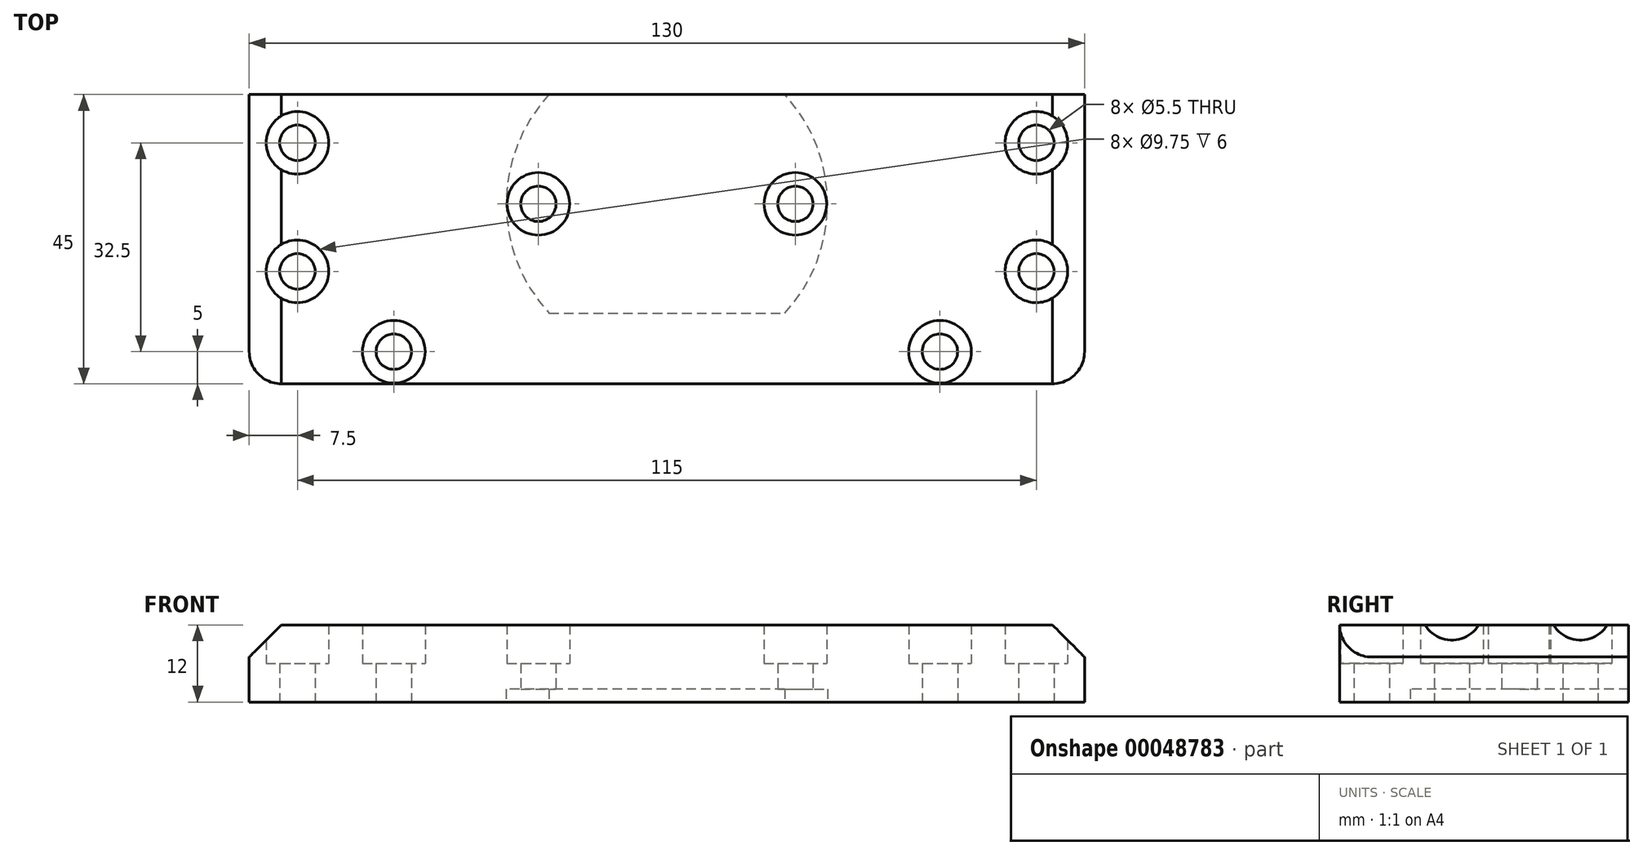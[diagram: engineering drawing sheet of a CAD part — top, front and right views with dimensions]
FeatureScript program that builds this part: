
annotation { "Feature Type Name" : "Feature", "Feature Type Description" : "" }
export const myFeature = defineFeature(function(context is Context, id is Id, definition is map)
    precondition{}
    {
        {
            var Q0;
            Q0=qCreatedBy(makeId("Top.planeOp"),FACE);
            var sketch = newSketch(context, id + "F0", { "sketchPlane" : qUnion([Q0])});
            skLineSegment(sketch, "E0.bottom", {"start": v(65, -22.5) * mm, "end": v(-65, -22.5) * mm});
            skLineSegment(sketch, "E0.top", {"start": v(65, 22.5) * mm, "end": v(-65, 22.5) * mm});
            skLineSegment(sketch, "E0.left", {"start": v(65, -22.5) * mm, "end": v(65, 22.5) * mm});
            skLineSegment(sketch, "E0.right", {"start": v(-65, -22.5) * mm, "end": v(-65, 22.5) * mm});
            skPoint(sketch, "E0.middle", {"position": v(0, 0) * mm});
            skSolve(sketch);
        }
        {
            var Q0;
            Q0=makeQuery(id+"F0.imprint","IMPRINT",FACE,{"disambiguationData":[TD([[makeQuery(id+"F0.imprint","IMPRINT",EDGE,{"derivedFrom":sQuery(id+"F0.wireOp",EDGE,"E0.bottom")}),-1.0]])]});
            extrude(context, id + "F1", {"entities" : qUnion([Q0]), "depth" : 12 * mm});
        }
        {
            var Q0;
            Q0=makeQuery(id+"F1.opExtrude","SWEPT_EDGE",EDGE,{"disambiguationData":[OSD([sQuery(id+"F0.wireOp",EDGE,"E0.bottom"),sQuery(id+"F0.wireOp",EDGE,"E0.left")])]});
            var Q1;
            Q1=makeQuery(id+"F1.opExtrude","SWEPT_EDGE",EDGE,{"disambiguationData":[OSD([sQuery(id+"F0.wireOp",EDGE,"E0.bottom"),sQuery(id+"F0.wireOp",EDGE,"E0.right")])]});
            fillet(context, id + "F2", {"entities" : qUnion([Q0, Q1]), "radius" : 5 * mm, "tangentPropagation" : true, "allowEdgeOverflow" : false});
        }
        {
            var Q0;
            Q0=makeQuery(id+"F1.opExtrude","CAP_FACE",FACE,{"disambiguationData":[OSD([sQuery(id+"F0.wireOp",EDGE,"E0.bottom"),sQuery(id+"F0.wireOp",EDGE,"E0.top"),sQuery(id+"F0.wireOp",EDGE,"E0.left"),sQuery(id+"F0.wireOp",EDGE,"E0.right")])],"isStart":false});
            var sketch = newSketch(context, id + "F3", { "sketchPlane" : qUnion([Q0])});
            skPoint(sketch, "E1", {"position": v(-57.5, -5) * mm});
            skPoint(sketch, "E2.0.1.0", {"position": v(-57.5, 15) * mm});
            skPoint(sketch, "E2.1.0.0", {"position": v(57.5, -5) * mm});
            skPoint(sketch, "E2.1.1.0", {"position": v(57.5, 15) * mm});
            skLineSegment(sketch, "E2.direction1", {"start": v(-57.5, -5) * mm, "end": v(57.5, -5) * mm, "construction": true});
            skLineSegment(sketch, "E2.direction2", {"start": v(-57.5, -5) * mm, "end": v(-57.5, 15) * mm, "construction": true});
            skPoint(sketch, "E3", {"position": v(-42.5, -17.5) * mm});
            skPoint(sketch, "E4.MirrorP", {"position": v(42.5, -17.5) * mm});
            skSolve(sketch);
        }
        {
            var Q0;
            Q0=makeQuery(id+"F1.opExtrude","CAP_FACE",FACE,{"disambiguationData":[OSD([sQuery(id+"F0.wireOp",EDGE,"E0.bottom"),sQuery(id+"F0.wireOp",EDGE,"E0.top"),sQuery(id+"F0.wireOp",EDGE,"E0.left"),sQuery(id+"F0.wireOp",EDGE,"E0.right")])],"isStart":false});
            var sketch = newSketch(context, id + "F4", { "sketchPlane" : qUnion([Q0])});
            skPoint(sketch, "E5", {"position": v(0, 5.5) * mm});
            skPoint(sketch, "E6", {"position": v(-20, 5.5) * mm});
            skPoint(sketch, "E7.MirrorP", {"position": v(20, 5.5) * mm});
            skSolve(sketch);
        }
        {
            var Q0;
            Q0=sQuery(id+"F3.wireOp",VERTEX,"E1");
            var Q1;
            Q1=sQuery(id+"F3.wireOp",VERTEX,"E2.0.1.0");
            var Q2;
            Q2=sQuery(id+"F3.wireOp",VERTEX,"E2.1.0.0");
            var Q3;
            Q3=sQuery(id+"F3.wireOp",VERTEX,"E2.1.1.0");
            var Q4;
            Q4=sQuery(id+"F3.wireOp",VERTEX,"E3");
            var Q5;
            Q5=sQuery(id+"F3.wireOp",VERTEX,"E4.MirrorP");
            var Q6;
            Q6=sQuery(id+"F4.wireOp",VERTEX,"E6");
            var Q7;
            Q7=sQuery(id+"F4.wireOp",VERTEX,"E7.MirrorP");
            var Q8;
            Q8=makeQuery(id+"F1.opExtrude","SWEPT_BODY",BODY,{"disambiguationData":[OSD([sQuery(id+"F0.wireOp",EDGE,"E0.bottom"),sQuery(id+"F0.wireOp",EDGE,"E0.top"),sQuery(id+"F0.wireOp",EDGE,"E0.left"),sQuery(id+"F0.wireOp",EDGE,"E0.right")])]});
            hole(context, id + "F5", {"style" : HoleStyle.C_BORE, "endStyle" : HoleEndStyle.THROUGH, "holeDiameter" : 5.5 * mm, "cBoreDiameter" : 9.75 * mm, "cBoreDepth" : 6 * mm, "locations" : qUnion([Q0, Q1, Q2, Q3, Q4, Q5, Q6, Q7]), "scope" : qUnion([Q8]), "isTappedThrough" : true, "startStyle" : HoleStartStyle.PART});
        }
        {
            var Q0;
            Q0=makeQuery(id+"F1.opExtrude","CAP_EDGE",EDGE,{"disambiguationData":[OSD([sQuery(id+"F0.wireOp",EDGE,"E0.right")])],"isStart":false});
            var Q1;
            Q1=makeQuery(id+"F1.opExtrude","CAP_EDGE",EDGE,{"disambiguationData":[OSD([sQuery(id+"F0.wireOp",EDGE,"E0.left")])],"isStart":false});
            chamfer(context, id + "F6", {"entities" : qUnion([Q0, Q1]), "width" : 5 * mm});
        }
        {
            var Q0;
            Q0=makeQuery(id+"F1.opExtrude","CAP_FACE",FACE,{"disambiguationData":[OSD([sQuery(id+"F0.wireOp",EDGE,"E0.bottom"),sQuery(id+"F0.wireOp",EDGE,"E0.top"),sQuery(id+"F0.wireOp",EDGE,"E0.left"),sQuery(id+"F0.wireOp",EDGE,"E0.right")])],"isStart":true});
            var sketch = newSketch(context, id + "F7", { "sketchPlane" : qUnion([Q0])});
            skPoint(sketch, "E8", {"position": v(0, -5.5) * mm});
            skLineSegment(sketch, "E9", {"start": v(-65, 11.5) * mm, "end": v(65, 11.5) * mm, "construction": true});
            skArc(sketch, "E10", {"start": v(18.33, -22.5) * mm, "mid": v(25, -5.5) * mm, "end": v(18.33, 11.5) * mm});
            skArc(sketch, "E11", {"start": v(-18.33, -22.5) * mm, "mid": v(-25, -5.5) * mm, "end": v(-18.33, 11.5) * mm});
            skLineSegment(sketch, "E12", {"start": v(-18.33, 11.5) * mm, "end": v(18.33, 11.5) * mm});
            skLineSegment(sketch, "E13", {"start": v(-18.33, -22.5) * mm, "end": v(18.33, -22.5) * mm});
            skSolve(sketch);
        }
        {
            var Q0;
            Q0=makeQuery(id+"F7.imprint","IMPRINT",FACE,{"disambiguationData":[TD([[makeQuery(id+"F7.imprint","IMPRINT",EDGE,{"derivedFrom":sQuery(id+"F7.wireOp",EDGE,"E10")}),1.0]])]});
            extrude(context, id + "F8", {"entities" : qUnion([Q0]), "operationType" : NewBodyOperationType.REMOVE, "oppositeDirection" : true, "depth" : 2 * mm});
        }
    });
